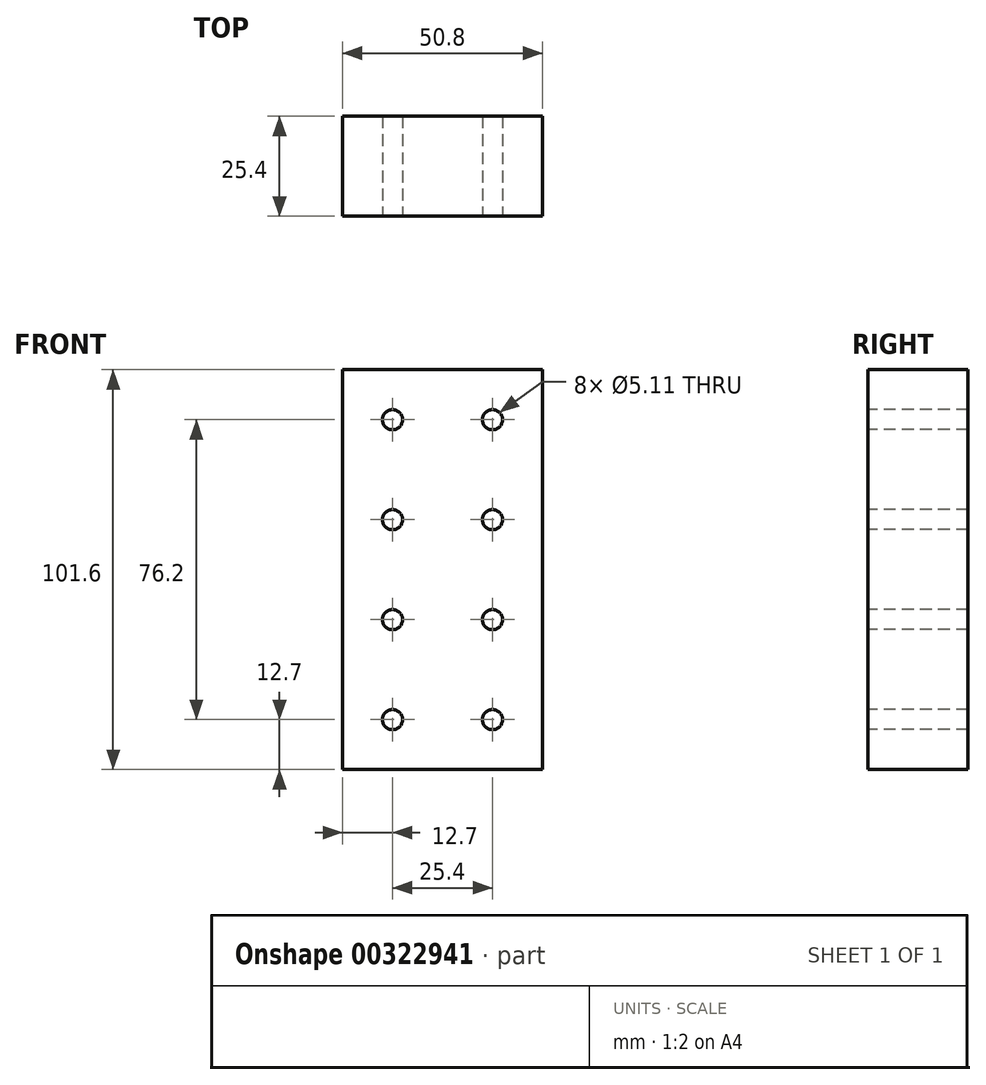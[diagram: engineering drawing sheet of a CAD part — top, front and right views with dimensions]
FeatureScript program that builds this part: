
annotation { "Feature Type Name" : "Feature", "Feature Type Description" : "" }
export const myFeature = defineFeature(function(context is Context, id is Id, definition is map)
    precondition{}
    {
        {
            var Q0;
            Q0=qCreatedBy(makeId("Front.planeOp"),FACE);
            var sketch = newSketch(context, id + "F0", { "sketchPlane" : qUnion([Q0])});
            skLineSegment(sketch, "E0.bottom", {"start": v(0, 0) * mm, "end": v(50.8, 0) * mm});
            skLineSegment(sketch, "E0.top", {"start": v(0, -101.6) * mm, "end": v(50.8, -101.6) * mm});
            skLineSegment(sketch, "E0.left", {"start": v(0, 0) * mm, "end": v(0, -101.6) * mm});
            skLineSegment(sketch, "E0.right", {"start": v(50.8, 0) * mm, "end": v(50.8, -101.6) * mm});
            skSolve(sketch);
        }
        {
            var Q0;
            Q0 = qSketchRegion(id + "F0", true);
            extrude(context, id + "F1", {"entities" : qUnion([Q0]), "depth" : 25.4 * mm});
        }
        {
            var Q0;
            Q0=makeQuery(id+"F1.opExtrude","CAP_FACE",FACE,{"disambiguationData":[OSD([sQuery(id+"F0.wireOp",EDGE,"E0.bottom"),sQuery(id+"F0.wireOp",EDGE,"E0.top"),sQuery(id+"F0.wireOp",EDGE,"E0.left"),sQuery(id+"F0.wireOp",EDGE,"E0.right")])],"isStart":false});
            var sketch = newSketch(context, id + "F2", { "sketchPlane" : qUnion([Q0])});
            skCircle(sketch, "E1", {"center": v(12.7, -12.7) * mm, "radius": 2.55 * mm});
            skCircle(sketch, "E2.0.1.0", {"center": v(12.7, -38.1) * mm, "radius": 2.55 * mm});
            skCircle(sketch, "E2.0.2.0", {"center": v(12.7, -63.5) * mm, "radius": 2.55 * mm});
            skCircle(sketch, "E2.0.3.0", {"center": v(12.7, -88.9) * mm, "radius": 2.55 * mm});
            skCircle(sketch, "E2.1.0.0", {"center": v(38.1, -12.7) * mm, "radius": 2.55 * mm});
            skCircle(sketch, "E2.1.1.0", {"center": v(38.1, -38.1) * mm, "radius": 2.55 * mm});
            skCircle(sketch, "E2.1.2.0", {"center": v(38.1, -63.5) * mm, "radius": 2.55 * mm});
            skCircle(sketch, "E2.1.3.0", {"center": v(38.1, -88.9) * mm, "radius": 2.55 * mm});
            skCircle(sketch, "E2.2.0.0", {"center": v(63.5, -12.7) * mm, "radius": 2.55 * mm});
            skCircle(sketch, "E2.2.1.0", {"center": v(63.5, -38.1) * mm, "radius": 2.55 * mm});
            skCircle(sketch, "E2.2.2.0", {"center": v(63.5, -63.5) * mm, "radius": 2.55 * mm});
            skCircle(sketch, "E2.2.3.0", {"center": v(63.5, -88.9) * mm, "radius": 2.55 * mm});
            skLineSegment(sketch, "E2.direction1", {"start": v(12.7, -12.7) * mm, "end": v(38.1, -12.7) * mm, "construction": true});
            skLineSegment(sketch, "E2.direction2", {"start": v(12.7, -12.7) * mm, "end": v(12.7, -38.1) * mm, "construction": true});
            skSolve(sketch);
        }
        {
            var Q0;
            Q0 = qSketchRegion(id + "F2", true);
            extrude(context, id + "F3", {"entities" : qUnion([Q0]), "operationType" : NewBodyOperationType.REMOVE, "oppositeDirection" : true, "depth" : 25.4 * mm});
        }
    });
